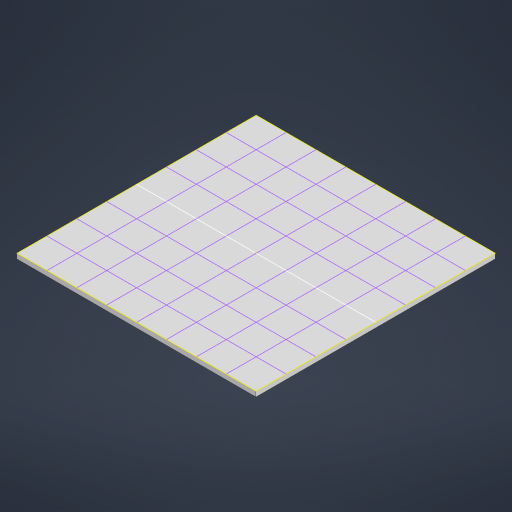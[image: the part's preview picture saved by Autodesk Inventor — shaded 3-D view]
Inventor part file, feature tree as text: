
AUTODESK INVENTOR PART (.ipt)
format: ipt  version: 2023 (Build 270158000, 158)  size: 178,176 bytes
history: native  units: mm
features: sketch x2, extrude x1
ambient origin geometry x8: Origin, YZ Plane, XZ Plane, XY Plane, X Axis, Y Axis, Z Axis, Center Point
bodies: Solid1 (feature_tree)
feature tree (3):
  extrude  "Extrusion1"  Depth=240.0mm
  sketch  "Sketch2"  dims[d2=5.0mm d3=0.0mm]
  sketch  "Sketch1"  dims[d0=240.0mm d1=240.0mm]
